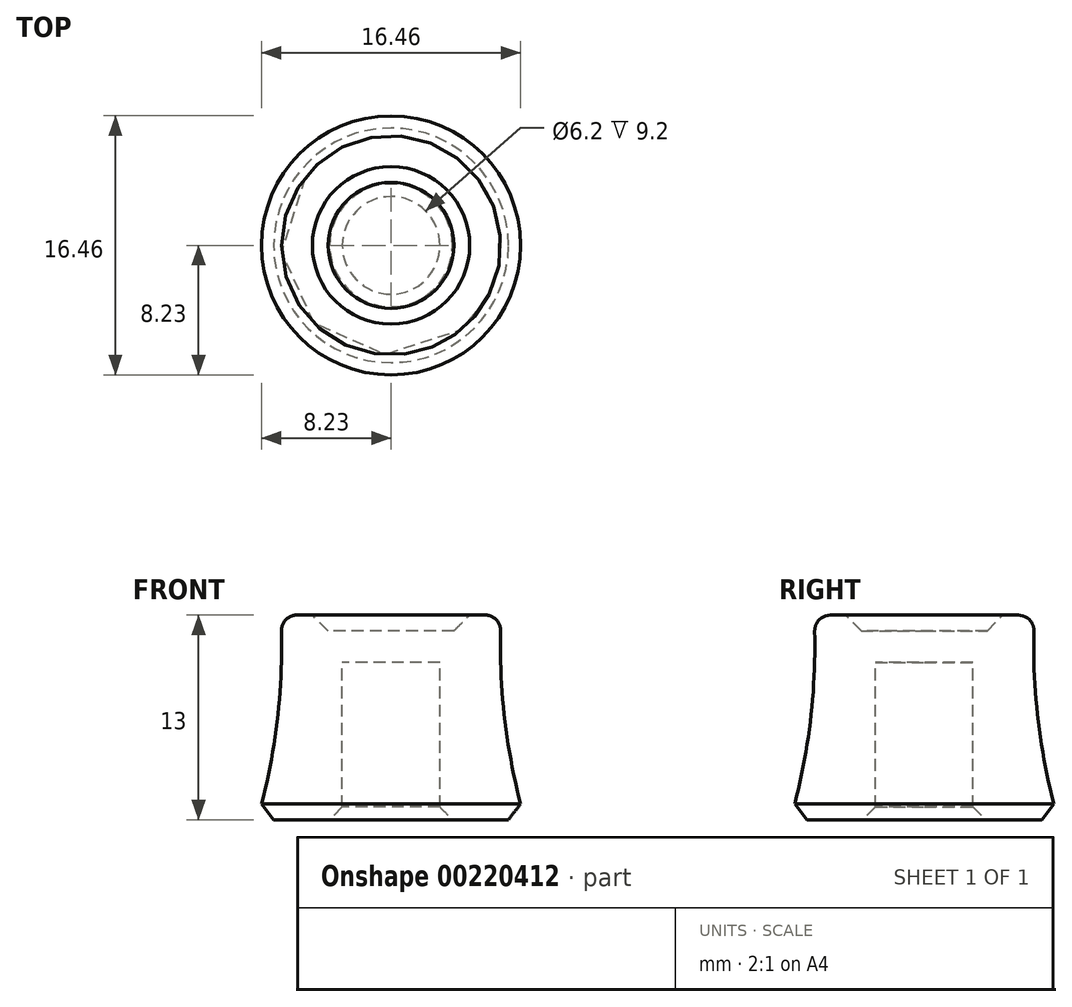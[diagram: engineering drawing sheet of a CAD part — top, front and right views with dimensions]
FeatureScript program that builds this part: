
annotation { "Feature Type Name" : "Feature", "Feature Type Description" : "" }
export const myFeature = defineFeature(function(context is Context, id is Id, definition is map)
    precondition{}
    {
        {
            var Q0;
            Q0=qCreatedBy(makeId("Front.planeOp"),FACE);
            var sketch = newSketch(context, id + "F0", { "sketchPlane" : qUnion([Q0])});
            skLineSegment(sketch, "E0", {"start": v(0, 10) * mm, "end": v(3.1, 10) * mm});
            skLineSegment(sketch, "E1", {"start": v(3.1, 10) * mm, "end": v(3.1, 0) * mm});
            skLineSegment(sketch, "E2", {"start": v(3.1, 0) * mm, "end": v(8.5, 0) * mm});
            skLineSegment(sketch, "E3", {"start": v(7, 13) * mm, "end": v(5, 13) * mm});
            skLineSegment(sketch, "E4", {"start": v(5, 13) * mm, "end": v(4, 12) * mm});
            skLineSegment(sketch, "E5", {"start": v(4, 12) * mm, "end": v(0, 12) * mm});
            skLineSegment(sketch, "E6", {"start": v(0, 12) * mm, "end": v(0, 10) * mm});
            skArc(sketch, "E7", {"start": v(7, 13) * mm, "mid": v(7.21, 6.44) * mm, "end": v(8.5, 0) * mm});
            skSolve(sketch);
        }
        {
            var Q0;
            Q0=makeQuery(id+"F0.imprint","IMPRINT",FACE,{"disambiguationData":[TD([[makeQuery(id+"F0.imprint","IMPRINT",EDGE,{"derivedFrom":sQuery(id+"F0.wireOp",EDGE,"E0")}),1.0]])]});
            var Q1;
            Q1=sQuery(id+"F0.wireOp",EDGE,"E6");
            revolve(context, id + "F1", {"entities" : qUnion([Q0]), "axis" : qUnion([Q1]), "revolveType" : RevolveType.FULL});
        }
        {
            var Q0;
            Q0=makeQuery(id+"F1.opRevolve","SWEPT_FACE",FACE,{"disambiguationData":[OSD([sQuery(id+"F0.wireOp",EDGE,"E5")])]});
            var sketch = newSketch(context, id + "F2", { "sketchPlane" : qUnion([Q0])});
            skArc(sketch, "E8", {"start": v(3.46, -2) * mm, "mid": v(0, 4) * mm, "end": v(-3.46, -2) * mm});
            skLineSegment(sketch, "E9", {"start": v(0, 0) * mm, "end": v(-3.46, -2) * mm, "construction": true});
            skLineSegment(sketch, "E10", {"start": v(0, 0) * mm, "end": v(3.46, -2) * mm, "construction": true});
            skLineSegment(sketch, "E11", {"start": v(0, 0) * mm, "end": v(0, -4.57) * mm, "construction": true});
            skArc(sketch, "E12", {"start": v(-2.42, -1.4) * mm, "mid": v(0, 2.8) * mm, "end": v(2.42, -1.4) * mm});
            skLineSegment(sketch, "E13", {"start": v(-2.42, -1.4) * mm, "end": v(-1.9, -1.1) * mm});
            skLineSegment(sketch, "E14", {"start": v(-1.9, -1.1) * mm, "end": v(-2.34, -2.74) * mm});
            skLineSegment(sketch, "E15", {"start": v(-2.34, -2.74) * mm, "end": v(-3.98, -2.3) * mm});
            skLineSegment(sketch, "E16", {"start": v(-3.98, -2.3) * mm, "end": v(-3.46, -2) * mm});
            skLineSegment(sketch, "E17", {"start": v(2.42, -1.4) * mm, "end": v(1.9, -1.1) * mm});
            skLineSegment(sketch, "E18", {"start": v(1.9, -1.1) * mm, "end": v(2.34, -2.74) * mm});
            skLineSegment(sketch, "E19", {"start": v(2.34, -2.74) * mm, "end": v(3.98, -2.3) * mm});
            skLineSegment(sketch, "E20", {"start": v(3.98, -2.3) * mm, "end": v(3.46, -2) * mm});
            skSolve(sketch);
        }
        {
            var Q0;
            Q0=makeQuery(id+"F1.opRevolve","SWEPT_EDGE",EDGE,{"disambiguationData":[OSD([sQuery(id+"F0.wireOp",EDGE,"E1"),sQuery(id+"F0.wireOp",EDGE,"E2")])]});
            var Q1;
            Q1=makeQuery(id+"F1.opRevolve","SWEPT_EDGE",EDGE,{"disambiguationData":[OSD([sQuery(id+"F0.wireOp",EDGE,"E2"),sQuery(id+"F0.wireOp",EDGE,"E7")])]});
            chamfer(context, id + "F3", {"entities" : qUnion([Q0, Q1]), "width" : 0.8 * mm, "tangentPropagation" : true});
        }
        {
            var Q0;
            Q0=makeQuery(id+"F1.opRevolve","SWEPT_EDGE",EDGE,{"disambiguationData":[OSD([sQuery(id+"F0.wireOp",EDGE,"E3"),sQuery(id+"F0.wireOp",EDGE,"E7")])]});
            fillet(context, id + "F4", {"entities" : qUnion([Q0]), "radius" : 1 * mm, "tangentPropagation" : true, "allowEdgeOverflow" : false});
        }
    });
